# Revit family: IS_ConnectSpace_E1327_BIM_DE
name_source: partatom
category: Generic Models
revit_build: Autodesk Revit MEP 2016 (Build: 20161004_0715(x64)
units: mm (PartAtom-declared; Revit-internal decimal feet)

## family parameters
Always vertical = No
Can host rebar = No
Cut with Voids When Loaded = No
Part Type = Normal
Room Calculation Point = No
Round Connector Dimension = Use Diameter
Shared = No
Work Plane-Based = No

## types (2) — shared parameters
BIMobject category = Basins
BOSUseNativeGeometries = 1
Brand url = http://www.idealstandard.co.uk
EAN code = https://5017830447627
Edition number = 1
IFC Classification = Sanitary Terminal
Installation instructions = http://www.idealstandard.it
Manufacturer name = Ideal Standard
Material main = Ceramics
NBS Reference Code = 35-79-18
NBS Reference Description = Counter Top Wash Basins
Nominal height = 175
Nominal width = 700
NominalHeight = 172 mm
NominalLength = 380 mm
NominalWidth = 700 mm  [stored 2.29659 ft]
OmniClass Code = 23-31 13 00
OmniClass Description = Sinks
Product Guid = 4738acde-3918-49bb-92d4-a64f77fb96a0
Product SKU = E1327
Product certification = http://www.idealstandard.it
Product data url = https://bimobject.com
Product family = CONNECT SPACE
Product group = Basin
Product name = CONNECT SPACE BASIN 70X38 WHITE LH PLTFRM
Product url = http://www.idealstandard.it
QR code = http://bimobject.com
Size = 700x380x172 mm
Technical description = http://www.idealstandard.it
Uniclass 1.4 Code = L7212
Uniclass 1.4 Description = Washbasins
Uniclass 2.0 Code = PR-35-79-94
Uniclass 2.0 Description = Wall-Hung Wash Basins
Uniclass 2015 Code = Pr_40_20_96_96
Uniclass 2015 Name = Wall-hung wash basins
Weight Net (Kg) = 16
Youtube clip = http://www.idealstandard.it
zero-valued in all types: DrainSize

## per-type parameters (varying)
| type | Model |
| E132701 CONNECT SPACE washbasin 700x380mm, 1 taphole, with overflow, left hand | E132701 |
| E1327MA CONNECT SPACE washbasin 700x380mm, 1 taphole, with overflow, left hand | E1327MA |

note: [stored X ft] marks values corroborated as IEEE doubles in the binary element streams (Revit-internal decimal feet)

## geometry (parser evidence)
native form markers: Blend x4, Sweep x1
no freeform markers — native parametric forms only
